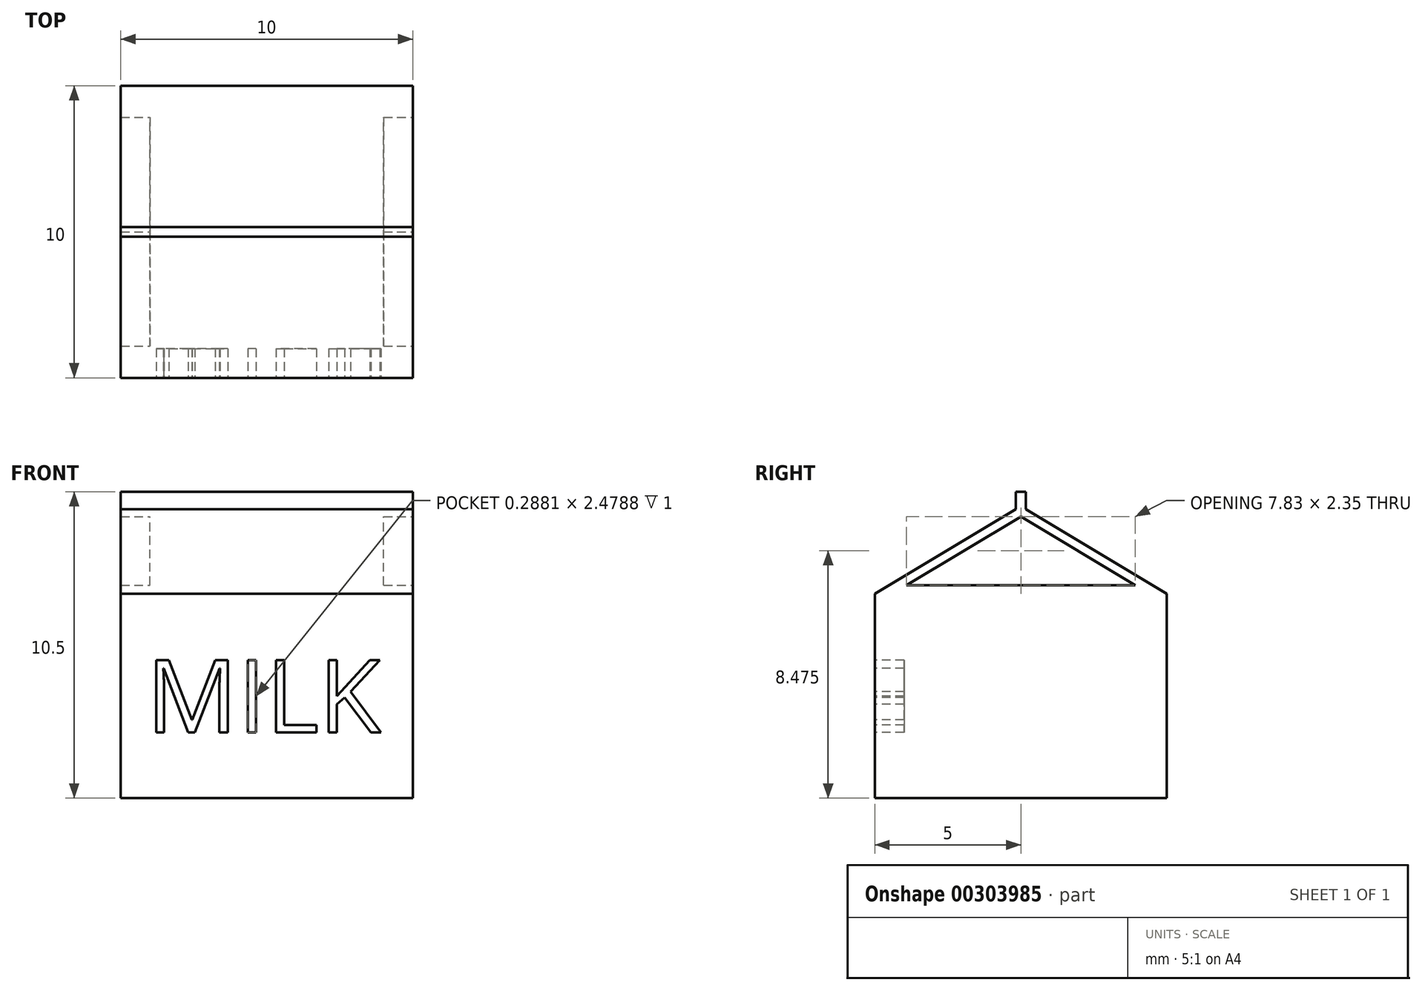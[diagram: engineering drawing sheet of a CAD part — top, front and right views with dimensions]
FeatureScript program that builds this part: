
annotation { "Feature Type Name" : "Feature", "Feature Type Description" : "" }
export const myFeature = defineFeature(function(context is Context, id is Id, definition is map)
    precondition{}
    {
        {
            var Q0;
            Q0=qCreatedBy(makeId("Top.planeOp"),FACE);
            var sketch = newSketch(context, id + "F0", { "sketchPlane" : qUnion([Q0])});
            skLineSegment(sketch, "E0.bottom", {"start": v(0, 0) * mm, "end": v(-10, 0) * mm});
            skLineSegment(sketch, "E0.top", {"start": v(0, 10) * mm, "end": v(-10, 10) * mm});
            skLineSegment(sketch, "E0.left", {"start": v(0, 0) * mm, "end": v(0, 10) * mm});
            skLineSegment(sketch, "E0.right", {"start": v(-10, 0) * mm, "end": v(-10, 10) * mm});
            skSolve(sketch);
        }
        {
            var Q0;
            Q0=makeQuery(id+"F0.imprint","IMPRINT",FACE,{"disambiguationData":[TD([[makeQuery(id+"F0.imprint","IMPRINT",EDGE,{"derivedFrom":sQuery(id+"F0.wireOp",EDGE,"E0.bottom")}),-1.0]])]});
            extrude(context, id + "F1", {"entities" : qUnion([Q0]), "depth" : 7 * mm});
        }
        {
            var Q0;
            Q0=makeQuery(id+"F1.opExtrude","SWEPT_FACE",FACE,{"disambiguationData":[OSD([sQuery(id+"F0.wireOp",EDGE,"E0.left")])]});
            var sketch = newSketch(context, id + "F2", { "sketchPlane" : qUnion([Q0])});
            skLineSegment(sketch, "E1", {"start": v(5, 7) * mm, "end": v(5, 10) * mm, "construction": true});
            skLineSegment(sketch, "E2", {"start": v(4.83, 9.9) * mm, "end": v(0, 7) * mm});
            skLineSegment(sketch, "E3", {"start": v(0, 7) * mm, "end": v(10, 7) * mm});
            skLineSegment(sketch, "E4", {"start": v(10, 7) * mm, "end": v(5.17, 9.9) * mm});
            skLineSegment(sketch, "E5", {"start": v(5.17, 9.9) * mm, "end": v(4.83, 9.9) * mm});
            skSolve(sketch);
        }
        {
            var Q0;
            Q0=makeQuery(id+"F2.imprint","IMPRINT",FACE,{"disambiguationData":[TD([[makeQuery(id+"F2.imprint","IMPRINT",EDGE,{"derivedFrom":sQuery(id+"F2.wireOp",EDGE,"E2")}),1.0]])]});
            extrude(context, id + "F3", {"entities" : qUnion([Q0]), "operationType" : NewBodyOperationType.ADD, "oppositeDirection" : true, "depth" : 10 * mm});
        }
        {
            var Q0;
            Q0=makeQuery(id+"F2.imprint","IMPRINT",FACE,{"disambiguationData":[TD([[makeQuery(id+"F2.imprint","IMPRINT",EDGE,{"derivedFrom":sQuery(id+"F2.wireOp",EDGE,"E2")}),1.0]])]});
            var sketch = newSketch(context, id + "F4", { "sketchPlane" : qUnion([Q0])});
            skLineSegment(sketch, "E6.0", {"start": v(5, 9.65) * mm, "end": v(1.08, 7.3) * mm});
            skLineSegment(sketch, "E6.1", {"start": v(8.92, 7.3) * mm, "end": v(5, 9.65) * mm});
            skLineSegment(sketch, "E6.2", {"start": v(1.08, 7.3) * mm, "end": v(8.92, 7.3) * mm});
            skSolve(sketch);
        }
        {
            var Q0;
            Q0 = qSketchRegion(id + "F4", true);
            extrude(context, id + "F5", {"entities" : qUnion([Q0]), "operationType" : NewBodyOperationType.REMOVE, "oppositeDirection" : true, "depth" : 25 * mm});
        }
        {
            var Q0;
            Q0=makeQuery(id+"F3.opExtrude","SWEPT_FACE",FACE,{"disambiguationData":[OSD([sQuery(id+"F2.wireOp",EDGE,"E5")])]});
            extrude(context, id + "F6", {"entities" : qUnion([Q0]), "operationType" : NewBodyOperationType.ADD, "depth" : .6 * mm});
        }
        {
            var Q0;
            Q0=makeQuery(id+"F1.opExtrude","SWEPT_FACE",FACE,{"disambiguationData":[OSD([sQuery(id+"F0.wireOp",EDGE,"E0.bottom")])]});
            var sketch = newSketch(context, id + "F7", { "sketchPlane" : qUnion([Q0])});
            skText(sketch, "E7", { "text": "MILK\n", "fontName": "OpenSans-Regular.ttf"});
            const initialGuessF7  = {"E7": [-0.00913, 0.00225, 1, 0, 0.0025]};
            skSetInitialGuess(sketch, initialGuessF7);
            skSolve(sketch);
        }
        {
            var Q0;
            Q0 = qSketchRegion(id + "F4", true);
            extrude(context, id + "F8", {"entities" : qUnion([Q0]), "operationType" : NewBodyOperationType.ADD, "oppositeDirection" : true, "depth" : 9 * mm});
        }
        {
            var Q0;
            Q0 = qSketchRegion(id + "F4", true);
            extrude(context, id + "F9", {"entities" : qUnion([Q0]), "operationType" : NewBodyOperationType.REMOVE, "oppositeDirection" : true, "depth" : 1 * mm});
        }
        {
            var Q0;
            Q0 = qSketchRegion(id + "F7", true);
            extrude(context, id + "F10", {"entities" : qUnion([Q0]), "operationType" : NewBodyOperationType.REMOVE, "oppositeDirection" : true, "depth" : 1 * mm});
        }
    });
